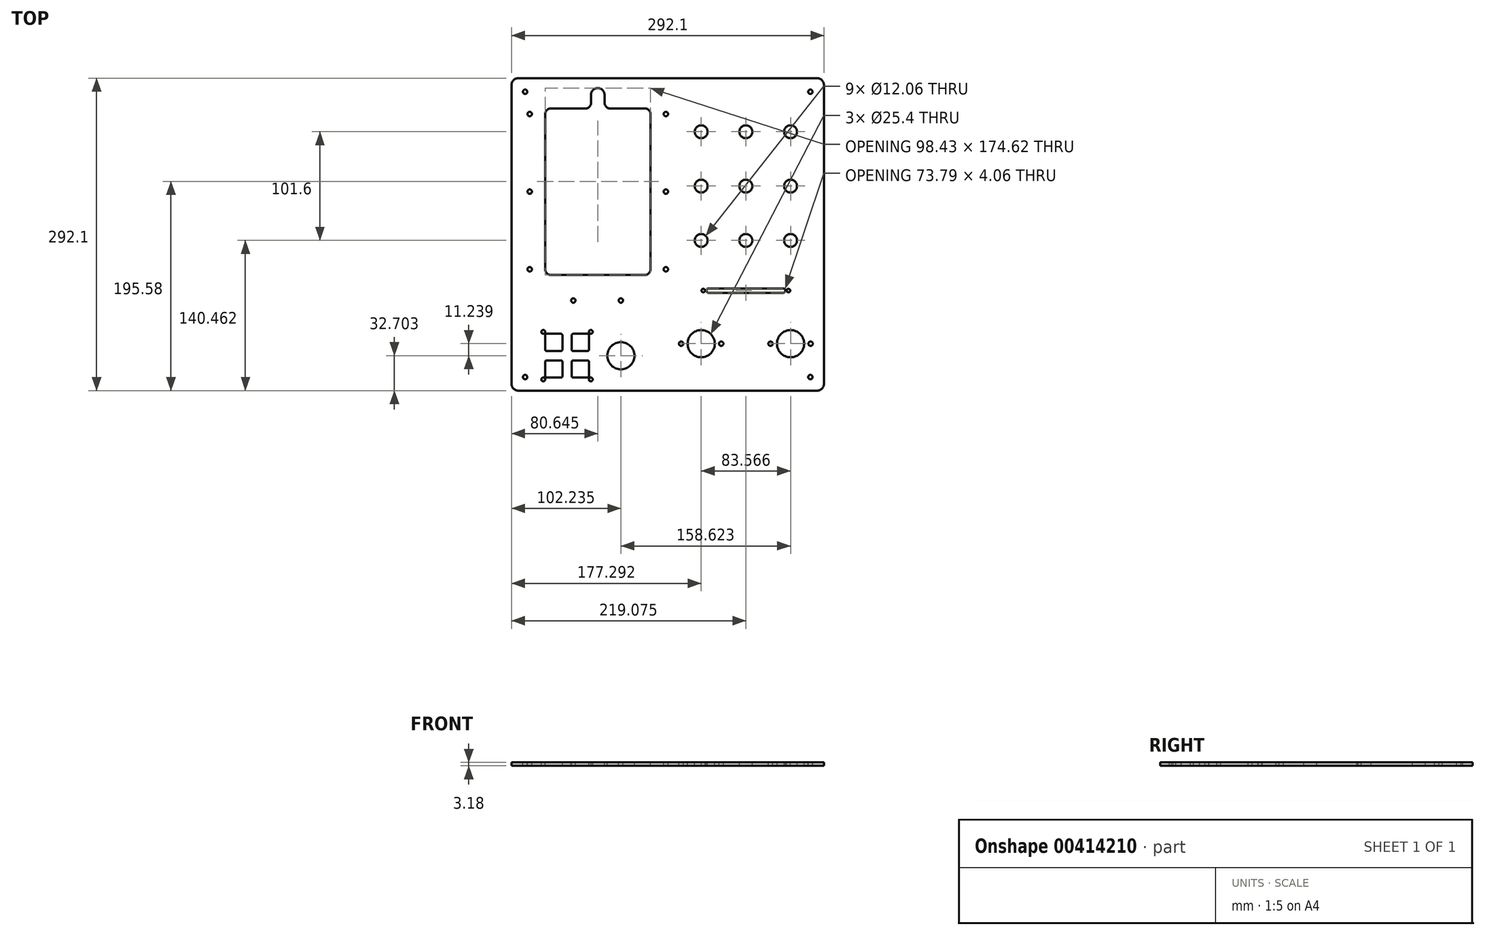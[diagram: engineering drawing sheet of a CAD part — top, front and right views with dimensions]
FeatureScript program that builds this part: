
annotation { "Feature Type Name" : "Feature", "Feature Type Description" : "" }
export const myFeature = defineFeature(function(context is Context, id is Id, definition is map)
    precondition{}
    {
        {
            var Q0;
            Q0=qCreatedBy(makeId("Top.planeOp"),FACE);
            var sketch = newSketch(context, id + "F0", { "sketchPlane" : qUnion([Q0])});
            skLineSegment(sketch, "E0.bottom", {"start": v(146.05, -146.05) * mm, "end": v(-146.05, -146.05) * mm});
            skLineSegment(sketch, "E0.top", {"start": v(146.05, 146.05) * mm, "end": v(-146.05, 146.05) * mm});
            skLineSegment(sketch, "E0.left", {"start": v(146.05, -146.05) * mm, "end": v(146.05, 146.05) * mm});
            skLineSegment(sketch, "E0.right", {"start": v(-146.05, -146.05) * mm, "end": v(-146.05, 146.05) * mm});
            skPoint(sketch, "E0.middle", {"position": v(0, 0) * mm});
            skCircle(sketch, "E1", {"center": v(-133.35, 133.35) * mm, "radius": 2.06 * mm});
            skLineSegment(sketch, "E2.bottom", {"start": v(-139.7, 139.7) * mm, "end": v(-6.35, 139.7) * mm, "construction": true});
            skLineSegment(sketch, "E2.top", {"start": v(-139.7, 6.35) * mm, "end": v(-6.35, 6.35) * mm, "construction": true});
            skLineSegment(sketch, "E2.left", {"start": v(-139.7, 139.7) * mm, "end": v(-139.7, 6.35) * mm, "construction": true});
            skLineSegment(sketch, "E2.right", {"start": v(-6.35, 139.7) * mm, "end": v(-6.35, 6.35) * mm, "construction": true});
            skLineSegment(sketch, "E3.bottom", {"start": v(6.35, 139.7) * mm, "end": v(139.7, 139.7) * mm, "construction": true});
            skLineSegment(sketch, "E3.top", {"start": v(6.35, 6.35) * mm, "end": v(139.7, 6.35) * mm, "construction": true});
            skLineSegment(sketch, "E3.left", {"start": v(6.35, 139.7) * mm, "end": v(6.35, 6.35) * mm, "construction": true});
            skLineSegment(sketch, "E3.right", {"start": v(139.7, 139.7) * mm, "end": v(139.7, 6.35) * mm, "construction": true});
            skLineSegment(sketch, "E4.bottom", {"start": v(-139.7, -6.35) * mm, "end": v(-6.35, -6.35) * mm, "construction": true});
            skLineSegment(sketch, "E4.top", {"start": v(-139.7, -139.7) * mm, "end": v(-6.35, -139.7) * mm, "construction": true});
            skLineSegment(sketch, "E4.left", {"start": v(-139.7, -6.35) * mm, "end": v(-139.7, -139.7) * mm, "construction": true});
            skLineSegment(sketch, "E4.right", {"start": v(-6.35, -6.35) * mm, "end": v(-6.35, -139.7) * mm, "construction": true});
            skLineSegment(sketch, "E5.bottom", {"start": v(6.35, -6.35) * mm, "end": v(139.7, -6.35) * mm, "construction": true});
            skLineSegment(sketch, "E5.top", {"start": v(6.35, -139.7) * mm, "end": v(139.7, -139.7) * mm, "construction": true});
            skLineSegment(sketch, "E5.left", {"start": v(6.35, -6.35) * mm, "end": v(6.35, -139.7) * mm, "construction": true});
            skLineSegment(sketch, "E5.right", {"start": v(139.7, -6.35) * mm, "end": v(139.7, -139.7) * mm, "construction": true});
            skCircle(sketch, "E6", {"center": v(-133.35, -133.35) * mm, "radius": 2.06 * mm});
            skCircle(sketch, "E7", {"center": v(133.35, -133.35) * mm, "radius": 2.06 * mm});
            skCircle(sketch, "E8", {"center": v(133.35, 133.35) * mm, "radius": 2.06 * mm});
            skSolve(sketch);
        }
        {
            var Q0;
            Q0 = qSketchRegion(id + "F0", true);
            extrude(context, id + "F1", {"entities" : qUnion([Q0]), "oppositeDirection" : true, "depth" : 3.17 * mm});
        }
        {
            var Q0;
            Q0=makeQuery(id+"F1.opExtrude","CAP_FACE",FACE,{"disambiguationData":[OSD([sQuery(id+"F0.wireOp",EDGE,"E0.bottom"),sQuery(id+"F0.wireOp",EDGE,"E0.top"),sQuery(id+"F0.wireOp",EDGE,"E0.left"),sQuery(id+"F0.wireOp",EDGE,"E0.right")])],"isStart":true});
            var sketch = newSketch(context, id + "F2", { "sketchPlane" : qUnion([Q0])});
            skLineSegment(sketch, "E9.bottom", {"start": v(-16.2, -37.78) * mm, "end": v(-114.62, -37.78) * mm});
            skLineSegment(sketch, "E9.left", {"start": v(-16.2, -37.78) * mm, "end": v(-16.2, 117.8) * mm});
            skLineSegment(sketch, "E9.right", {"start": v(-114.62, -37.78) * mm, "end": v(-114.62, 117.8) * mm});
            skPoint(sketch, "E9.middle", {"position": v(-65.4, 40) * mm});
            skLineSegment(sketch, "E10", {"start": v(-114.62, 117.8) * mm, "end": v(-71.75, 117.8) * mm});
            skLineSegment(sketch, "E11", {"start": v(-16.2, 117.8) * mm, "end": v(-59.05, 117.8) * mm});
            skLineSegment(sketch, "E12", {"start": v(-71.75, 117.8) * mm, "end": v(-59.05, 117.8) * mm, "construction": true});
            skLineSegment(sketch, "E13.bottom", {"start": v(-5.08, -58.42) * mm, "end": v(-125.73, -58.42) * mm, "construction": true});
            skLineSegment(sketch, "E13.top", {"start": v(-5.08, 138.43) * mm, "end": v(-125.73, 138.43) * mm, "construction": true});
            skLineSegment(sketch, "E13.left", {"start": v(-5.08, -58.42) * mm, "end": v(-5.08, 138.43) * mm, "construction": true});
            skLineSegment(sketch, "E14", {"start": v(-71.75, -58.42) * mm, "end": v(-71.75, -101.6) * mm, "construction": true});
            skLineSegment(sketch, "E15", {"start": v(-71.75, -101.6) * mm, "end": v(-59.05, -101.6) * mm, "construction": true});
            skLineSegment(sketch, "E16", {"start": v(-59.05, -101.6) * mm, "end": v(-59.05, -58.42) * mm, "construction": true});
            skPoint(sketch, "E17", {"position": v(-65.4, -58.42) * mm});
            skPoint(sketch, "E18", {"position": v(-65.4, -101.6) * mm});
            skLineSegment(sketch, "E19", {"start": v(-15.87, -58.42) * mm, "end": v(-15.87, -101.6) * mm, "construction": true});
            skLineSegment(sketch, "E20", {"start": v(-15.87, -101.6) * mm, "end": v(-28.57, -101.6) * mm, "construction": true});
            skLineSegment(sketch, "E21", {"start": v(-28.57, -101.6) * mm, "end": v(-28.57, -58.42) * mm, "construction": true});
            skPoint(sketch, "E22", {"position": v(-22.22, -101.6) * mm});
            skPoint(sketch, "E23", {"position": v(-22.22, -58.42) * mm});
            skLineSegment(sketch, "E24.bottom", {"start": v(-69.09, -138.43) * mm, "end": v(-119.25, -138.43) * mm, "construction": true});
            skLineSegment(sketch, "E24.top", {"start": v(-69.09, -88.27) * mm, "end": v(-119.25, -88.27) * mm, "construction": true});
            skLineSegment(sketch, "E24.left", {"start": v(-69.09, -138.43) * mm, "end": v(-69.09, -88.26) * mm, "construction": true});
            skLineSegment(sketch, "E24.right", {"start": v(-119.25, -138.43) * mm, "end": v(-119.25, -88.26) * mm, "construction": true});
            skPoint(sketch, "E24.middle", {"position": v(-94.17, -113.35) * mm});
            skCircle(sketch, "E25", {"center": v(-116.4, -91.12) * mm, "radius": 1.78 * mm});
            skCircle(sketch, "E26", {"center": v(-71.95, -91.12) * mm, "radius": 1.78 * mm});
            skCircle(sketch, "E27", {"center": v(-71.95, -135.57) * mm, "radius": 1.78 * mm});
            skCircle(sketch, "E28", {"center": v(-116.4, -135.57) * mm, "radius": 1.78 * mm});
            skLineSegment(sketch, "E29", {"start": v(-116.4, -91.12) * mm, "end": v(-71.95, -91.12) * mm, "construction": true});
            skLineSegment(sketch, "E30", {"start": v(-116.4, -91.12) * mm, "end": v(-116.4, -135.57) * mm, "construction": true});
            skPoint(sketch, "E31", {"position": v(-94.17, -91.12) * mm});
            skPoint(sketch, "E32", {"position": v(-116.4, -113.35) * mm});
            skLineSegment(sketch, "E33.bottom", {"start": v(-98.54, -108.98) * mm, "end": v(-114.62, -108.98) * mm});
            skLineSegment(sketch, "E33.top", {"start": v(-98.54, -92.9) * mm, "end": v(-114.62, -92.9) * mm});
            skLineSegment(sketch, "E33.left", {"start": v(-98.54, -108.98) * mm, "end": v(-98.54, -92.9) * mm});
            skLineSegment(sketch, "E33.right", {"start": v(-114.62, -108.98) * mm, "end": v(-114.62, -92.9) * mm});
            skPoint(sketch, "E33.middle", {"position": v(-106.58, -100.94) * mm});
            skLineSegment(sketch, "E34.bottom", {"start": v(-73.72, -108.98) * mm, "end": v(-89.8, -108.98) * mm});
            skLineSegment(sketch, "E34.top", {"start": v(-73.72, -92.9) * mm, "end": v(-89.8, -92.9) * mm});
            skLineSegment(sketch, "E34.left", {"start": v(-73.72, -108.98) * mm, "end": v(-73.72, -92.9) * mm});
            skLineSegment(sketch, "E34.right", {"start": v(-89.8, -108.98) * mm, "end": v(-89.8, -92.9) * mm});
            skPoint(sketch, "E34.middle", {"position": v(-81.76, -100.94) * mm});
            skLineSegment(sketch, "E35.bottom", {"start": v(-98.54, -133.8) * mm, "end": v(-114.62, -133.8) * mm});
            skLineSegment(sketch, "E35.top", {"start": v(-98.54, -117.72) * mm, "end": v(-114.62, -117.72) * mm});
            skLineSegment(sketch, "E35.left", {"start": v(-98.54, -133.8) * mm, "end": v(-98.54, -117.72) * mm});
            skLineSegment(sketch, "E35.right", {"start": v(-114.62, -133.8) * mm, "end": v(-114.62, -117.72) * mm});
            skPoint(sketch, "E35.middle", {"position": v(-106.58, -125.76) * mm});
            skLineSegment(sketch, "E36.bottom", {"start": v(-73.72, -133.8) * mm, "end": v(-89.8, -133.8) * mm});
            skLineSegment(sketch, "E36.top", {"start": v(-73.72, -117.72) * mm, "end": v(-89.8, -117.72) * mm});
            skLineSegment(sketch, "E36.left", {"start": v(-73.72, -133.8) * mm, "end": v(-73.72, -117.72) * mm});
            skLineSegment(sketch, "E36.right", {"start": v(-89.8, -133.8) * mm, "end": v(-89.8, -117.72) * mm});
            skPoint(sketch, "E36.middle", {"position": v(-81.76, -125.76) * mm});
            skLineSegment(sketch, "E37", {"start": v(-106.58, -100.94) * mm, "end": v(-81.76, -100.94) * mm, "construction": true});
            skLineSegment(sketch, "E38", {"start": v(-106.58, -100.94) * mm, "end": v(-106.58, -125.76) * mm, "construction": true});
            skPoint(sketch, "E39", {"position": v(-94.17, -100.94) * mm});
            skPoint(sketch, "E40", {"position": v(-106.58, -113.35) * mm});
            skLineSegment(sketch, "E41", {"start": v(-114.62, -27.37) * mm, "end": v(-16.2, -27.37) * mm, "construction": true});
            skCircle(sketch, "E42", {"center": v(-129.06, -32.58) * mm, "radius": 2.06 * mm});
            skCircle(sketch, "E43", {"center": v(-1.75, -32.58) * mm, "radius": 2.06 * mm});
            skLineSegment(sketch, "E44", {"start": v(-129.06, -32.58) * mm, "end": v(-129.06, -27.37) * mm, "construction": true});
            skLineSegment(sketch, "E45", {"start": v(-129.06, -27.37) * mm, "end": v(-114.62, -27.37) * mm, "construction": true});
            skLineSegment(sketch, "E46", {"start": v(-16.2, -27.37) * mm, "end": v(-1.75, -27.37) * mm, "construction": true});
            skLineSegment(sketch, "E47", {"start": v(-1.75, -27.37) * mm, "end": v(-1.75, -32.58) * mm, "construction": true});
            skLineSegment(sketch, "E48", {"start": v(-71.75, 117.8) * mm, "end": v(-71.75, 130.5) * mm});
            skLineSegment(sketch, "E49", {"start": v(-59.05, 117.8) * mm, "end": v(-59.05, 130.5) * mm});
            skArc(sketch, "E50", {"start": v(-71.75, 130.5) * mm, "mid": v(-65.4, 136.84) * mm, "end": v(-59.05, 130.5) * mm});
            skCircle(sketch, "E51", {"center": v(31.24, -102.1) * mm, "radius": 12.7 * mm});
            skLineSegment(sketch, "E52.bottom", {"start": v(56.13, -127) * mm, "end": v(6.35, -127) * mm, "construction": true});
            skLineSegment(sketch, "E52.top", {"start": v(56.13, -77.22) * mm, "end": v(6.35, -77.22) * mm, "construction": true});
            skLineSegment(sketch, "E52.left", {"start": v(56.13, -127) * mm, "end": v(56.13, -77.22) * mm, "construction": true});
            skLineSegment(sketch, "E52.right", {"start": v(6.35, -127) * mm, "end": v(6.35, -77.22) * mm, "construction": true});
            skLineSegment(sketch, "E53.bottom", {"start": v(-139.7, 139.7) * mm, "end": v(-6.35, 139.7) * mm, "construction": true});
            skLineSegment(sketch, "E53.top", {"start": v(-139.7, 6.35) * mm, "end": v(-6.35, 6.35) * mm, "construction": true});
            skLineSegment(sketch, "E53.left", {"start": v(-139.7, 139.7) * mm, "end": v(-139.7, 6.35) * mm, "construction": true});
            skLineSegment(sketch, "E53.right", {"start": v(-6.35, 139.7) * mm, "end": v(-6.35, 6.35) * mm, "construction": true});
            skLineSegment(sketch, "E54.bottom", {"start": v(139.7, 139.7) * mm, "end": v(6.35, 139.7) * mm, "construction": true});
            skLineSegment(sketch, "E54.top", {"start": v(139.7, 6.35) * mm, "end": v(6.35, 6.35) * mm, "construction": true});
            skLineSegment(sketch, "E54.left", {"start": v(139.7, 139.7) * mm, "end": v(139.7, 6.35) * mm, "construction": true});
            skLineSegment(sketch, "E54.right", {"start": v(6.35, 139.7) * mm, "end": v(6.35, 6.35) * mm, "construction": true});
            skLineSegment(sketch, "E55.bottom", {"start": v(-139.7, -139.7) * mm, "end": v(-6.35, -139.7) * mm, "construction": true});
            skLineSegment(sketch, "E55.top", {"start": v(-139.7, -6.35) * mm, "end": v(-6.35, -6.35) * mm, "construction": true});
            skLineSegment(sketch, "E55.left", {"start": v(-139.7, -139.7) * mm, "end": v(-139.7, -6.35) * mm, "construction": true});
            skLineSegment(sketch, "E55.right", {"start": v(-6.35, -139.7) * mm, "end": v(-6.35, -6.35) * mm, "construction": true});
            skLineSegment(sketch, "E56.bottom", {"start": v(6.35, -6.35) * mm, "end": v(139.7, -6.35) * mm, "construction": true});
            skLineSegment(sketch, "E56.top", {"start": v(6.35, -139.7) * mm, "end": v(139.7, -139.7) * mm, "construction": true});
            skLineSegment(sketch, "E56.left", {"start": v(6.35, -6.35) * mm, "end": v(6.35, -139.7) * mm, "construction": true});
            skLineSegment(sketch, "E56.right", {"start": v(139.7, -6.35) * mm, "end": v(139.7, -139.7) * mm, "construction": true});
            skLineSegment(sketch, "E57.bottom", {"start": v(139.7, 139.7) * mm, "end": v(127, 139.7) * mm, "construction": true});
            skLineSegment(sketch, "E57.top", {"start": v(139.7, 127) * mm, "end": v(127, 127) * mm, "construction": true});
            skLineSegment(sketch, "E57.left", {"start": v(139.7, 139.7) * mm, "end": v(139.7, 127) * mm, "construction": true});
            skLineSegment(sketch, "E57.right", {"start": v(127, 139.7) * mm, "end": v(127, 127) * mm, "construction": true});
            skLineSegment(sketch, "E58", {"start": v(19.05, 139.7) * mm, "end": v(19.05, 127) * mm, "construction": true});
            skLineSegment(sketch, "E59", {"start": v(19.05, 127) * mm, "end": v(6.35, 127) * mm, "construction": true});
            skLineSegment(sketch, "E60", {"start": v(6.35, 19.05) * mm, "end": v(19.05, 19.05) * mm, "construction": true});
            skLineSegment(sketch, "E61", {"start": v(19.05, 19.05) * mm, "end": v(19.05, 6.35) * mm, "construction": true});
            skLineSegment(sketch, "E62", {"start": v(127, 6.35) * mm, "end": v(127, 19.05) * mm, "construction": true});
            skLineSegment(sketch, "E63", {"start": v(127, 19.05) * mm, "end": v(139.7, 19.05) * mm, "construction": true});
            skLineSegment(sketch, "E64", {"start": v(-127, 139.7) * mm, "end": v(-127, 127) * mm, "construction": true});
            skLineSegment(sketch, "E65", {"start": v(-127, 127) * mm, "end": v(-139.7, 127) * mm, "construction": true});
            skLineSegment(sketch, "E66", {"start": v(-139.7, 19.05) * mm, "end": v(-127, 19.05) * mm, "construction": true});
            skLineSegment(sketch, "E67", {"start": v(-127, 19.05) * mm, "end": v(-127, 6.35) * mm, "construction": true});
            skLineSegment(sketch, "E68", {"start": v(-19.05, 139.7) * mm, "end": v(-19.05, 127) * mm, "construction": true});
            skLineSegment(sketch, "E69", {"start": v(-19.05, 127) * mm, "end": v(-6.35, 127) * mm, "construction": true});
            skLineSegment(sketch, "E70", {"start": v(-6.35, 19.05) * mm, "end": v(-19.05, 19.05) * mm, "construction": true});
            skLineSegment(sketch, "E71", {"start": v(-19.05, 19.05) * mm, "end": v(-19.05, 6.35) * mm, "construction": true});
            skLineSegment(sketch, "E72", {"start": v(-139.7, -19.05) * mm, "end": v(-127, -19.05) * mm, "construction": true});
            skLineSegment(sketch, "E73", {"start": v(-127, -19.05) * mm, "end": v(-127, -6.35) * mm, "construction": true});
            skLineSegment(sketch, "E74", {"start": v(-19.05, -6.35) * mm, "end": v(-19.05, -19.05) * mm, "construction": true});
            skLineSegment(sketch, "E75", {"start": v(-19.05, -19.05) * mm, "end": v(-6.35, -19.05) * mm, "construction": true});
            skLineSegment(sketch, "E76", {"start": v(-127, -127) * mm, "end": v(-127, -139.7) * mm, "construction": true});
            skLineSegment(sketch, "E77", {"start": v(-19.05, -139.7) * mm, "end": v(-19.05, -127) * mm, "construction": true});
            skLineSegment(sketch, "E78", {"start": v(-19.05, -127) * mm, "end": v(-6.35, -127) * mm, "construction": true});
            skLineSegment(sketch, "E79", {"start": v(6.35, -19.05) * mm, "end": v(19.05, -19.05) * mm, "construction": true});
            skLineSegment(sketch, "E80", {"start": v(19.05, -19.05) * mm, "end": v(19.05, -6.35) * mm, "construction": true});
            skLineSegment(sketch, "E81", {"start": v(127, -6.35) * mm, "end": v(127, -19.05) * mm, "construction": true});
            skLineSegment(sketch, "E82", {"start": v(127, -19.05) * mm, "end": v(139.7, -19.05) * mm, "construction": true});
            skLineSegment(sketch, "E83", {"start": v(6.35, -127) * mm, "end": v(19.05, -127) * mm, "construction": true});
            skLineSegment(sketch, "E84", {"start": v(19.05, -127) * mm, "end": v(19.05, -139.7) * mm, "construction": true});
            skLineSegment(sketch, "E85", {"start": v(127, -139.7) * mm, "end": v(127, -127) * mm, "construction": true});
            skLineSegment(sketch, "E86", {"start": v(127, -127) * mm, "end": v(139.7, -127) * mm, "construction": true});
            skCircle(sketch, "E87", {"center": v(114.8, -102.1) * mm, "radius": 12.7 * mm});
            skLineSegment(sketch, "E88.bottom", {"start": v(139.7, -127) * mm, "end": v(89.92, -127) * mm, "construction": true});
            skLineSegment(sketch, "E88.top", {"start": v(139.7, -77.22) * mm, "end": v(89.92, -77.22) * mm, "construction": true});
            skLineSegment(sketch, "E88.left", {"start": v(139.7, -127) * mm, "end": v(139.7, -77.22) * mm, "construction": true});
            skLineSegment(sketch, "E88.right", {"start": v(89.92, -127) * mm, "end": v(89.92, -77.22) * mm, "construction": true});
            skCircle(sketch, "E89", {"center": v(31.24, 96.01) * mm, "radius": 6.03 * mm});
            skLineSegment(sketch, "E90.bottom", {"start": v(39.27, 81.91) * mm, "end": v(23.2, 81.91) * mm, "construction": true});
            skLineSegment(sketch, "E90.top", {"start": v(39.27, 110.1) * mm, "end": v(23.2, 110.1) * mm, "construction": true});
            skLineSegment(sketch, "E90.left", {"start": v(39.27, 81.91) * mm, "end": v(39.27, 110.1) * mm, "construction": true});
            skLineSegment(sketch, "E90.right", {"start": v(23.2, 81.91) * mm, "end": v(23.2, 110.1) * mm, "construction": true});
            skLineSegment(sketch, "E91", {"start": v(37.6, 71.75) * mm, "end": v(31.24, 71.75) * mm, "construction": true});
            skLineSegment(sketch, "E92", {"start": v(31.24, 71.75) * mm, "end": v(31.24, 81.91) * mm, "construction": true});
            skLineSegment(sketch, "E93", {"start": v(37.6, 71.75) * mm, "end": v(37.6, 81.91) * mm, "construction": true});
            skPoint(sketch, "E94.0.1.0", {"position": v(31.24, 45.21) * mm});
            skLineSegment(sketch, "E94.0.1.1", {"start": v(37.6, 20.95) * mm, "end": v(31.24, 20.95) * mm, "construction": true});
            skLineSegment(sketch, "E94.0.1.2", {"start": v(37.6, 20.95) * mm, "end": v(37.6, 31.11) * mm, "construction": true});
            skLineSegment(sketch, "E94.0.1.3", {"start": v(31.24, 20.95) * mm, "end": v(31.24, 31.11) * mm, "construction": true});
            skLineSegment(sketch, "E94.0.1.4", {"start": v(23.2, 31.11) * mm, "end": v(23.2, 59.3) * mm, "construction": true});
            skLineSegment(sketch, "E94.0.1.5", {"start": v(39.27, 31.11) * mm, "end": v(39.27, 59.3) * mm, "construction": true});
            skLineSegment(sketch, "E94.0.1.6", {"start": v(39.27, 59.3) * mm, "end": v(23.2, 59.3) * mm, "construction": true});
            skLineSegment(sketch, "E94.0.1.7", {"start": v(39.27, 31.11) * mm, "end": v(23.2, 31.11) * mm, "construction": true});
            skCircle(sketch, "E94.0.1.8", {"center": v(31.24, 45.21) * mm, "radius": 6.03 * mm});
            skPoint(sketch, "E94.0.2.0", {"position": v(31.24, -5.59) * mm});
            skLineSegment(sketch, "E94.0.2.1", {"start": v(37.6, -29.84) * mm, "end": v(31.24, -29.84) * mm, "construction": true});
            skLineSegment(sketch, "E94.0.2.2", {"start": v(37.6, -29.84) * mm, "end": v(37.6, -19.68) * mm, "construction": true});
            skLineSegment(sketch, "E94.0.2.3", {"start": v(31.24, -29.84) * mm, "end": v(31.24, -19.68) * mm, "construction": true});
            skLineSegment(sketch, "E94.0.2.4", {"start": v(23.2, -19.68) * mm, "end": v(23.2, 8.5) * mm, "construction": true});
            skLineSegment(sketch, "E94.0.2.5", {"start": v(39.27, -19.68) * mm, "end": v(39.27, 8.5) * mm, "construction": true});
            skLineSegment(sketch, "E94.0.2.6", {"start": v(39.27, 8.5) * mm, "end": v(23.2, 8.5) * mm, "construction": true});
            skLineSegment(sketch, "E94.0.2.7", {"start": v(39.27, -19.68) * mm, "end": v(23.2, -19.68) * mm, "construction": true});
            skCircle(sketch, "E94.0.2.8", {"center": v(31.24, -5.59) * mm, "radius": 6.03 * mm});
            skPoint(sketch, "E94.1.0.0", {"position": v(73.02, 96.01) * mm});
            skLineSegment(sketch, "E94.1.0.1", {"start": v(79.38, 71.75) * mm, "end": v(73.03, 71.75) * mm, "construction": true});
            skLineSegment(sketch, "E94.1.0.2", {"start": v(79.38, 71.75) * mm, "end": v(79.38, 81.91) * mm, "construction": true});
            skLineSegment(sketch, "E94.1.0.3", {"start": v(73.03, 71.75) * mm, "end": v(73.03, 81.91) * mm, "construction": true});
            skLineSegment(sketch, "E94.1.0.4", {"start": v(65, 81.91) * mm, "end": v(65, 110.1) * mm, "construction": true});
            skLineSegment(sketch, "E94.1.0.5", {"start": v(81.06, 81.91) * mm, "end": v(81.06, 110.1) * mm, "construction": true});
            skLineSegment(sketch, "E94.1.0.6", {"start": v(81.06, 110.1) * mm, "end": v(65, 110.1) * mm, "construction": true});
            skLineSegment(sketch, "E94.1.0.7", {"start": v(81.06, 81.91) * mm, "end": v(65, 81.91) * mm, "construction": true});
            skCircle(sketch, "E94.1.0.8", {"center": v(73.02, 96.01) * mm, "radius": 6.03 * mm});
            skPoint(sketch, "E94.1.1.0", {"position": v(73.02, 45.21) * mm});
            skLineSegment(sketch, "E94.1.1.1", {"start": v(79.38, 20.95) * mm, "end": v(73.03, 20.95) * mm, "construction": true});
            skLineSegment(sketch, "E94.1.1.2", {"start": v(79.38, 20.95) * mm, "end": v(79.38, 31.11) * mm, "construction": true});
            skLineSegment(sketch, "E94.1.1.3", {"start": v(73.03, 20.95) * mm, "end": v(73.03, 31.11) * mm, "construction": true});
            skLineSegment(sketch, "E94.1.1.4", {"start": v(65, 31.11) * mm, "end": v(65, 59.3) * mm, "construction": true});
            skLineSegment(sketch, "E94.1.1.5", {"start": v(81.06, 31.11) * mm, "end": v(81.06, 59.3) * mm, "construction": true});
            skLineSegment(sketch, "E94.1.1.6", {"start": v(81.06, 59.3) * mm, "end": v(65, 59.3) * mm, "construction": true});
            skLineSegment(sketch, "E94.1.1.7", {"start": v(81.06, 31.11) * mm, "end": v(65, 31.11) * mm, "construction": true});
            skCircle(sketch, "E94.1.1.8", {"center": v(73.02, 45.21) * mm, "radius": 6.03 * mm});
            skPoint(sketch, "E94.1.2.0", {"position": v(73.02, -5.59) * mm});
            skLineSegment(sketch, "E94.1.2.1", {"start": v(79.38, -29.84) * mm, "end": v(73.03, -29.84) * mm, "construction": true});
            skLineSegment(sketch, "E94.1.2.2", {"start": v(79.38, -29.84) * mm, "end": v(79.38, -19.68) * mm, "construction": true});
            skLineSegment(sketch, "E94.1.2.3", {"start": v(73.03, -29.84) * mm, "end": v(73.03, -19.68) * mm, "construction": true});
            skLineSegment(sketch, "E94.1.2.4", {"start": v(65, -19.68) * mm, "end": v(65, 8.5) * mm, "construction": true});
            skLineSegment(sketch, "E94.1.2.5", {"start": v(81.06, -19.68) * mm, "end": v(81.06, 8.5) * mm, "construction": true});
            skLineSegment(sketch, "E94.1.2.6", {"start": v(81.06, 8.5) * mm, "end": v(65, 8.5) * mm, "construction": true});
            skLineSegment(sketch, "E94.1.2.7", {"start": v(81.06, -19.68) * mm, "end": v(65, -19.68) * mm, "construction": true});
            skCircle(sketch, "E94.1.2.8", {"center": v(73.02, -5.59) * mm, "radius": 6.03 * mm});
            skPoint(sketch, "E94.2.0.0", {"position": v(114.8, 96.01) * mm});
            skLineSegment(sketch, "E94.2.0.1", {"start": v(121.16, 71.75) * mm, "end": v(114.8, 71.75) * mm, "construction": true});
            skLineSegment(sketch, "E94.2.0.2", {"start": v(121.16, 71.75) * mm, "end": v(121.16, 81.91) * mm, "construction": true});
            skLineSegment(sketch, "E94.2.0.3", {"start": v(114.8, 71.75) * mm, "end": v(114.8, 81.91) * mm, "construction": true});
            skLineSegment(sketch, "E94.2.0.4", {"start": v(106.78, 81.91) * mm, "end": v(106.78, 110.1) * mm, "construction": true});
            skLineSegment(sketch, "E94.2.0.5", {"start": v(122.84, 81.91) * mm, "end": v(122.84, 110.1) * mm, "construction": true});
            skLineSegment(sketch, "E94.2.0.6", {"start": v(122.84, 110.1) * mm, "end": v(106.78, 110.1) * mm, "construction": true});
            skLineSegment(sketch, "E94.2.0.7", {"start": v(122.84, 81.91) * mm, "end": v(106.78, 81.91) * mm, "construction": true});
            skCircle(sketch, "E94.2.0.8", {"center": v(114.8, 96.01) * mm, "radius": 6.03 * mm});
            skPoint(sketch, "E94.2.1.0", {"position": v(114.8, 45.21) * mm});
            skLineSegment(sketch, "E94.2.1.1", {"start": v(121.16, 20.95) * mm, "end": v(114.8, 20.95) * mm, "construction": true});
            skLineSegment(sketch, "E94.2.1.2", {"start": v(121.16, 20.95) * mm, "end": v(121.16, 31.11) * mm, "construction": true});
            skLineSegment(sketch, "E94.2.1.3", {"start": v(114.8, 20.95) * mm, "end": v(114.8, 31.11) * mm, "construction": true});
            skLineSegment(sketch, "E94.2.1.4", {"start": v(106.78, 31.11) * mm, "end": v(106.78, 59.3) * mm, "construction": true});
            skLineSegment(sketch, "E94.2.1.5", {"start": v(122.84, 31.11) * mm, "end": v(122.84, 59.3) * mm, "construction": true});
            skLineSegment(sketch, "E94.2.1.6", {"start": v(122.84, 59.3) * mm, "end": v(106.78, 59.3) * mm, "construction": true});
            skLineSegment(sketch, "E94.2.1.7", {"start": v(122.84, 31.11) * mm, "end": v(106.78, 31.11) * mm, "construction": true});
            skCircle(sketch, "E94.2.1.8", {"center": v(114.8, 45.21) * mm, "radius": 6.03 * mm});
            skPoint(sketch, "E94.2.2.0", {"position": v(114.8, -5.59) * mm});
            skLineSegment(sketch, "E94.2.2.1", {"start": v(121.16, -29.84) * mm, "end": v(114.8, -29.84) * mm, "construction": true});
            skLineSegment(sketch, "E94.2.2.2", {"start": v(121.16, -29.84) * mm, "end": v(121.16, -19.68) * mm, "construction": true});
            skLineSegment(sketch, "E94.2.2.3", {"start": v(114.8, -29.84) * mm, "end": v(114.8, -19.68) * mm, "construction": true});
            skLineSegment(sketch, "E94.2.2.4", {"start": v(106.78, -19.68) * mm, "end": v(106.78, 8.5) * mm, "construction": true});
            skLineSegment(sketch, "E94.2.2.5", {"start": v(122.84, -19.68) * mm, "end": v(122.84, 8.5) * mm, "construction": true});
            skLineSegment(sketch, "E94.2.2.6", {"start": v(122.84, 8.5) * mm, "end": v(106.78, 8.5) * mm, "construction": true});
            skLineSegment(sketch, "E94.2.2.7", {"start": v(122.84, -19.68) * mm, "end": v(106.78, -19.68) * mm, "construction": true});
            skCircle(sketch, "E94.2.2.8", {"center": v(114.8, -5.59) * mm, "radius": 6.03 * mm});
            skLineSegment(sketch, "E94.direction1", {"start": v(31.24, 71.75) * mm, "end": v(73.03, 71.75) * mm, "construction": true});
            skLineSegment(sketch, "E94.direction2", {"start": v(31.24, 71.75) * mm, "end": v(31.24, 20.95) * mm, "construction": true});
            skLineSegment(sketch, "E95", {"start": v(-127, -127) * mm, "end": v(-139.7, -127) * mm, "construction": true});
            skLineSegment(sketch, "E96", {"start": v(-125.73, -58.42) * mm, "end": v(-125.73, 138.43) * mm, "construction": true});
            skPoint(sketch, "E97", {"position": v(-65.4, 117.8) * mm});
            skPoint(sketch, "E98", {"position": v(-65.4, -27.37) * mm});
            skLineSegment(sketch, "E99", {"start": v(-65.4, 117.8) * mm, "end": v(-65.4, -27.37) * mm, "construction": true});
            skPoint(sketch, "E100", {"position": v(-65.4, 45.21) * mm});
            skLineSegment(sketch, "E101", {"start": v(-59.05, -101.6) * mm, "end": v(-28.57, -101.6) * mm, "construction": true});
            skPoint(sketch, "E102", {"position": v(-43.81, -101.6) * mm});
            skCircle(sketch, "E103", {"center": v(-43.81, -113.35) * mm, "radius": 12.7 * mm});
            skCircle(sketch, "E104", {"center": v(12.52, -102.1) * mm, "radius": 2.03 * mm});
            skCircle(sketch, "E105", {"center": v(49.97, -102.1) * mm, "radius": 2.03 * mm});
            skCircle(sketch, "E106", {"center": v(96.08, -102.1) * mm, "radius": 2.03 * mm});
            skCircle(sketch, "E107", {"center": v(133.53, -102.1) * mm, "radius": 2.03 * mm});
            skLineSegment(sketch, "E108", {"start": v(12.52, -102.1) * mm, "end": v(31.24, -102.1) * mm, "construction": true});
            skLineSegment(sketch, "E109", {"start": v(31.24, -102.1) * mm, "end": v(49.97, -102.1) * mm, "construction": true});
            skLineSegment(sketch, "E110", {"start": v(96.08, -102.1) * mm, "end": v(114.8, -102.1) * mm, "construction": true});
            skLineSegment(sketch, "E111", {"start": v(114.8, -102.1) * mm, "end": v(133.53, -102.1) * mm, "construction": true});
            skCircle(sketch, "E112", {"center": v(-129.06, 112.59) * mm, "radius": 2.06 * mm});
            skCircle(sketch, "E113", {"center": v(-1.75, 112.59) * mm, "radius": 2.06 * mm});
            skLineSegment(sketch, "E114", {"start": v(-129.06, 112.59) * mm, "end": v(-1.75, 112.59) * mm, "construction": true});
            skLineSegment(sketch, "E115", {"start": v(-1.75, 112.59) * mm, "end": v(-1.75, -32.58) * mm, "construction": true});
            skLineSegment(sketch, "E116", {"start": v(-129.06, 112.59) * mm, "end": v(-129.06, -32.58) * mm, "construction": true});
            skCircle(sketch, "E117", {"center": v(-129.06, 40) * mm, "radius": 2.06 * mm});
            skCircle(sketch, "E118", {"center": v(-1.75, 40) * mm, "radius": 2.06 * mm});
            skLineSegment(sketch, "E119.bottom", {"start": v(28.94, -40.46) * mm, "end": v(117.11, -40.46) * mm, "construction": true});
            skLineSegment(sketch, "E119.top", {"start": v(28.94, -64.52) * mm, "end": v(117.11, -64.52) * mm, "construction": true});
            skLineSegment(sketch, "E119.left", {"start": v(28.94, -40.46) * mm, "end": v(28.94, -64.52) * mm, "construction": true});
            skLineSegment(sketch, "E119.right", {"start": v(117.11, -40.46) * mm, "end": v(117.11, -64.52) * mm, "construction": true});
            skLineSegment(sketch, "E120", {"start": v(56.13, -77.22) * mm, "end": v(89.92, -77.22) * mm, "construction": true});
            skPoint(sketch, "E121", {"position": v(73.03, -77.22) * mm});
            skPoint(sketch, "E122", {"position": v(73.03, -64.52) * mm});
            skPoint(sketch, "E123", {"position": v(28.94, -52.49) * mm});
            skPoint(sketch, "E124", {"position": v(117.11, -52.49) * mm});
            skLineSegment(sketch, "E125", {"start": v(28.94, -52.49) * mm, "end": v(33.2, -52.49) * mm, "construction": true});
            skLineSegment(sketch, "E126", {"start": v(112.85, -52.49) * mm, "end": v(117.11, -52.49) * mm, "construction": true});
            skCircle(sketch, "E127", {"center": v(33.2, -52.49) * mm, "radius": 1.65 * mm});
            skCircle(sketch, "E128", {"center": v(112.85, -52.49) * mm, "radius": 1.65 * mm});
            skLineSegment(sketch, "E129", {"start": v(-125.73, -61.75) * mm, "end": v(-88.27, -61.75) * mm, "construction": true});
            skLineSegment(sketch, "E130", {"start": v(-88.27, -61.75) * mm, "end": v(-43.81, -61.75) * mm, "construction": true});
            skLineSegment(sketch, "E131", {"start": v(-43.81, -61.75) * mm, "end": v(-6.35, -61.75) * mm, "construction": true});
            skCircle(sketch, "E132", {"center": v(-88.27, -61.75) * mm, "radius": 2.06 * mm});
            skCircle(sketch, "E133", {"center": v(-43.81, -61.75) * mm, "radius": 2.06 * mm});
            skLineSegment(sketch, "E134", {"start": v(-127, -32.58) * mm, "end": v(-125.73, -32.58) * mm, "construction": true});
            skLineSegment(sketch, "E135", {"start": v(-88.27, -59.7) * mm, "end": v(-88.27, -58.42) * mm, "construction": true});
            skLineSegment(sketch, "E136", {"start": v(36.13, -50.46) * mm, "end": v(109.92, -50.46) * mm});
            skLineSegment(sketch, "E137", {"start": v(36.13, -54.52) * mm, "end": v(109.92, -54.52) * mm});
            skLineSegment(sketch, "E138", {"start": v(36.13, -50.46) * mm, "end": v(36.13, -54.52) * mm});
            skLineSegment(sketch, "E139", {"start": v(109.92, -50.46) * mm, "end": v(109.92, -54.52) * mm});
            skPoint(sketch, "E140", {"position": v(73.03, -40.46) * mm});
            skPoint(sketch, "E141", {"position": v(73.03, -50.46) * mm});
            skPoint(sketch, "E142", {"position": v(36.13, -52.49) * mm});
            skSolve(sketch);
        }
        {
            var Q0;
            Q0 = qSketchRegion(id + "F2", true);
            extrude(context, id + "F3", {"entities" : qUnion([Q0]), "operationType" : NewBodyOperationType.REMOVE, "endBound" : BoundingType.THROUGH_ALL, "oppositeDirection" : true, "depth" : 25.4 * mm});
        }
        {
            var Q0;
            Q0=makeQuery(id+"F3.boolean.opBoolean","COPY",EDGE,{"derivedFrom":makeQuery(id+"F3.opExtrude","SWEPT_EDGE",EDGE,{"disambiguationData":[OSD([sQuery(id+"F2.wireOp",EDGE,"E9.right"),sQuery(id+"F2.wireOp",EDGE,"E10")])]})});
            var Q1;
            Q1=makeQuery(id+"F3.boolean.opBoolean","COPY",EDGE,{"derivedFrom":makeQuery(id+"F3.opExtrude","SWEPT_EDGE",EDGE,{"disambiguationData":[OSD([sQuery(id+"F2.wireOp",EDGE,"E9.left"),sQuery(id+"F2.wireOp",EDGE,"E11")])]})});
            var Q2;
            Q2=makeQuery(id+"F3.boolean.opBoolean","COPY",EDGE,{"derivedFrom":makeQuery(id+"F3.opExtrude","SWEPT_EDGE",EDGE,{"disambiguationData":[OSD([sQuery(id+"F2.wireOp",EDGE,"E9.bottom"),sQuery(id+"F2.wireOp",EDGE,"E9.left")])]})});
            var Q3;
            Q3=makeQuery(id+"F3.boolean.opBoolean","COPY",EDGE,{"derivedFrom":makeQuery(id+"F3.opExtrude","SWEPT_EDGE",EDGE,{"disambiguationData":[OSD([sQuery(id+"F2.wireOp",EDGE,"E9.bottom"),sQuery(id+"F2.wireOp",EDGE,"E9.right")])]})});
            var Q4;
            Q4=makeQuery(id+"F3.boolean.opBoolean","COPY",EDGE,{"derivedFrom":makeQuery(id+"F3.opExtrude","SWEPT_EDGE",EDGE,{"disambiguationData":[OSD([sQuery(id+"F2.wireOp",EDGE,"E10"),sQuery(id+"F2.wireOp",EDGE,"BO560liI-brGj-X4hG-Arjd-MUWlCnzGjzVF")])]})});
            var Q5;
            Q5=makeQuery(id+"F3.boolean.opBoolean","COPY",EDGE,{"derivedFrom":makeQuery(id+"F3.opExtrude","SWEPT_EDGE",EDGE,{"disambiguationData":[OSD([sQuery(id+"F2.wireOp",EDGE,"E11"),sQuery(id+"F2.wireOp",EDGE,"BO560liI-brGj-X4hG-Arjd-MUWlCnzGjzVF")])]})});
            fillet(context, id + "F4", {"entities" : qUnion([Q0, Q1, Q2, Q3, Q4, Q5]), "radius" : 5.08 * mm, "tangentPropagation" : true, "allowEdgeOverflow" : false});
        }
        {
            var Q0;
            Q0=makeQuery(id+"F3.boolean.opBoolean","COPY",EDGE,{"derivedFrom":makeQuery(id+"F3.opExtrude","SWEPT_EDGE",EDGE,{"disambiguationData":[OSD([sQuery(id+"F2.wireOp",EDGE,"E33.top"),sQuery(id+"F2.wireOp",EDGE,"E33.right")])]})});
            var Q1;
            Q1=makeQuery(id+"F3.boolean.opBoolean","COPY",EDGE,{"derivedFrom":makeQuery(id+"F3.opExtrude","SWEPT_EDGE",EDGE,{"disambiguationData":[OSD([sQuery(id+"F2.wireOp",EDGE,"E34.top"),sQuery(id+"F2.wireOp",EDGE,"E34.right")])]})});
            var Q2;
            Q2=makeQuery(id+"F3.boolean.opBoolean","COPY",EDGE,{"derivedFrom":makeQuery(id+"F3.opExtrude","SWEPT_EDGE",EDGE,{"disambiguationData":[OSD([sQuery(id+"F2.wireOp",EDGE,"E36.top"),sQuery(id+"F2.wireOp",EDGE,"E36.right")])]})});
            var Q3;
            Q3=makeQuery(id+"F3.boolean.opBoolean","COPY",EDGE,{"derivedFrom":makeQuery(id+"F3.opExtrude","SWEPT_EDGE",EDGE,{"disambiguationData":[OSD([sQuery(id+"F2.wireOp",EDGE,"E35.top"),sQuery(id+"F2.wireOp",EDGE,"E35.right")])]})});
            var Q4;
            Q4=makeQuery(id+"F3.boolean.opBoolean","COPY",EDGE,{"derivedFrom":makeQuery(id+"F3.opExtrude","SWEPT_EDGE",EDGE,{"disambiguationData":[OSD([sQuery(id+"F2.wireOp",EDGE,"E33.top"),sQuery(id+"F2.wireOp",EDGE,"E33.left")])]})});
            var Q5;
            Q5=makeQuery(id+"F3.boolean.opBoolean","COPY",EDGE,{"derivedFrom":makeQuery(id+"F3.opExtrude","SWEPT_EDGE",EDGE,{"disambiguationData":[OSD([sQuery(id+"F2.wireOp",EDGE,"E34.top"),sQuery(id+"F2.wireOp",EDGE,"E34.left")])]})});
            var Q6;
            Q6=makeQuery(id+"F3.boolean.opBoolean","COPY",EDGE,{"derivedFrom":makeQuery(id+"F3.opExtrude","SWEPT_EDGE",EDGE,{"disambiguationData":[OSD([sQuery(id+"F2.wireOp",EDGE,"E35.top"),sQuery(id+"F2.wireOp",EDGE,"E35.left")])]})});
            var Q7;
            Q7=makeQuery(id+"F3.boolean.opBoolean","COPY",EDGE,{"derivedFrom":makeQuery(id+"F3.opExtrude","SWEPT_EDGE",EDGE,{"disambiguationData":[OSD([sQuery(id+"F2.wireOp",EDGE,"E36.top"),sQuery(id+"F2.wireOp",EDGE,"E36.left")])]})});
            var Q8;
            Q8=makeQuery(id+"F3.boolean.opBoolean","COPY",EDGE,{"derivedFrom":makeQuery(id+"F3.opExtrude","SWEPT_EDGE",EDGE,{"disambiguationData":[OSD([sQuery(id+"F2.wireOp",EDGE,"E36.bottom"),sQuery(id+"F2.wireOp",EDGE,"E36.left")])]})});
            var Q9;
            Q9=makeQuery(id+"F3.boolean.opBoolean","COPY",EDGE,{"derivedFrom":makeQuery(id+"F3.opExtrude","SWEPT_EDGE",EDGE,{"disambiguationData":[OSD([sQuery(id+"F2.wireOp",EDGE,"E34.bottom"),sQuery(id+"F2.wireOp",EDGE,"E34.left")])]})});
            var Q10;
            Q10=makeQuery(id+"F3.boolean.opBoolean","COPY",EDGE,{"derivedFrom":makeQuery(id+"F3.opExtrude","SWEPT_EDGE",EDGE,{"disambiguationData":[OSD([sQuery(id+"F2.wireOp",EDGE,"E33.bottom"),sQuery(id+"F2.wireOp",EDGE,"E33.left")])]})});
            var Q11;
            Q11=makeQuery(id+"F3.boolean.opBoolean","COPY",EDGE,{"derivedFrom":makeQuery(id+"F3.opExtrude","SWEPT_EDGE",EDGE,{"disambiguationData":[OSD([sQuery(id+"F2.wireOp",EDGE,"E35.bottom"),sQuery(id+"F2.wireOp",EDGE,"E35.left")])]})});
            var Q12;
            Q12=makeQuery(id+"F3.boolean.opBoolean","COPY",EDGE,{"derivedFrom":makeQuery(id+"F3.opExtrude","SWEPT_EDGE",EDGE,{"disambiguationData":[OSD([sQuery(id+"F2.wireOp",EDGE,"E35.bottom"),sQuery(id+"F2.wireOp",EDGE,"E35.right")])]})});
            var Q13;
            Q13=makeQuery(id+"F3.boolean.opBoolean","COPY",EDGE,{"derivedFrom":makeQuery(id+"F3.opExtrude","SWEPT_EDGE",EDGE,{"disambiguationData":[OSD([sQuery(id+"F2.wireOp",EDGE,"E33.bottom"),sQuery(id+"F2.wireOp",EDGE,"E33.right")])]})});
            var Q14;
            Q14=makeQuery(id+"F3.boolean.opBoolean","COPY",EDGE,{"derivedFrom":makeQuery(id+"F3.opExtrude","SWEPT_EDGE",EDGE,{"disambiguationData":[OSD([sQuery(id+"F2.wireOp",EDGE,"E34.bottom"),sQuery(id+"F2.wireOp",EDGE,"E34.right")])]})});
            var Q15;
            Q15=makeQuery(id+"F3.boolean.opBoolean","COPY",EDGE,{"derivedFrom":makeQuery(id+"F3.opExtrude","SWEPT_EDGE",EDGE,{"disambiguationData":[OSD([sQuery(id+"F2.wireOp",EDGE,"E36.bottom"),sQuery(id+"F2.wireOp",EDGE,"E36.right")])]})});
            fillet(context, id + "F5", {"entities" : qUnion([Q0, Q1, Q2, Q3, Q4, Q5, Q6, Q7, Q8, Q9, Q10, Q11, Q12, Q13, Q14, Q15]), "radius" : 1.27 * mm, "tangentPropagation" : true, "allowEdgeOverflow" : false});
        }
        {
            var Q0;
            Q0=makeQuery(id+"F1.opExtrude","SWEPT_EDGE",EDGE,{"disambiguationData":[OSD([sQuery(id+"F0.wireOp",EDGE,"E0.top"),sQuery(id+"F0.wireOp",EDGE,"E0.right")])]});
            var Q1;
            Q1=makeQuery(id+"F1.opExtrude","SWEPT_EDGE",EDGE,{"disambiguationData":[OSD([sQuery(id+"F0.wireOp",EDGE,"E0.top"),sQuery(id+"F0.wireOp",EDGE,"E0.left")])]});
            var Q2;
            Q2=makeQuery(id+"F1.opExtrude","SWEPT_EDGE",EDGE,{"disambiguationData":[OSD([sQuery(id+"F0.wireOp",EDGE,"E0.bottom"),sQuery(id+"F0.wireOp",EDGE,"E0.left")])]});
            var Q3;
            Q3=makeQuery(id+"F1.opExtrude","SWEPT_EDGE",EDGE,{"disambiguationData":[OSD([sQuery(id+"F0.wireOp",EDGE,"E0.bottom"),sQuery(id+"F0.wireOp",EDGE,"E0.right")])]});
            fillet(context, id + "F6", {"entities" : qUnion([Q0, Q1, Q2, Q3]), "radius" : 6.35 * mm, "tangentPropagation" : true, "allowEdgeOverflow" : false});
        }
        {
            var Q0;
            Q0=makeQuery(id+"F3.boolean.opBoolean","COPY",EDGE,{"derivedFrom":makeQuery(id+"F3.opExtrude","SWEPT_EDGE",EDGE,{"disambiguationData":[OSD([sQuery(id+"F2.wireOp",EDGE,"E136"),sQuery(id+"F2.wireOp",EDGE,"E138")])]})});
            var Q1;
            Q1=makeQuery(id+"F3.boolean.opBoolean","COPY",EDGE,{"derivedFrom":makeQuery(id+"F3.opExtrude","SWEPT_EDGE",EDGE,{"disambiguationData":[OSD([sQuery(id+"F2.wireOp",EDGE,"E136"),sQuery(id+"F2.wireOp",EDGE,"E139")])]})});
            var Q2;
            Q2=makeQuery(id+"F3.boolean.opBoolean","COPY",EDGE,{"derivedFrom":makeQuery(id+"F3.opExtrude","SWEPT_EDGE",EDGE,{"disambiguationData":[OSD([sQuery(id+"F2.wireOp",EDGE,"E137"),sQuery(id+"F2.wireOp",EDGE,"E139")])]})});
            var Q3;
            Q3=makeQuery(id+"F3.boolean.opBoolean","COPY",EDGE,{"derivedFrom":makeQuery(id+"F3.opExtrude","SWEPT_EDGE",EDGE,{"disambiguationData":[OSD([sQuery(id+"F2.wireOp",EDGE,"E137"),sQuery(id+"F2.wireOp",EDGE,"E138")])]})});
            fillet(context, id + "F7", {"entities" : qUnion([Q0, Q1, Q2, Q3]), "radius" : 1.78 * mm, "tangentPropagation" : true, "allowEdgeOverflow" : false});
        }
    });
